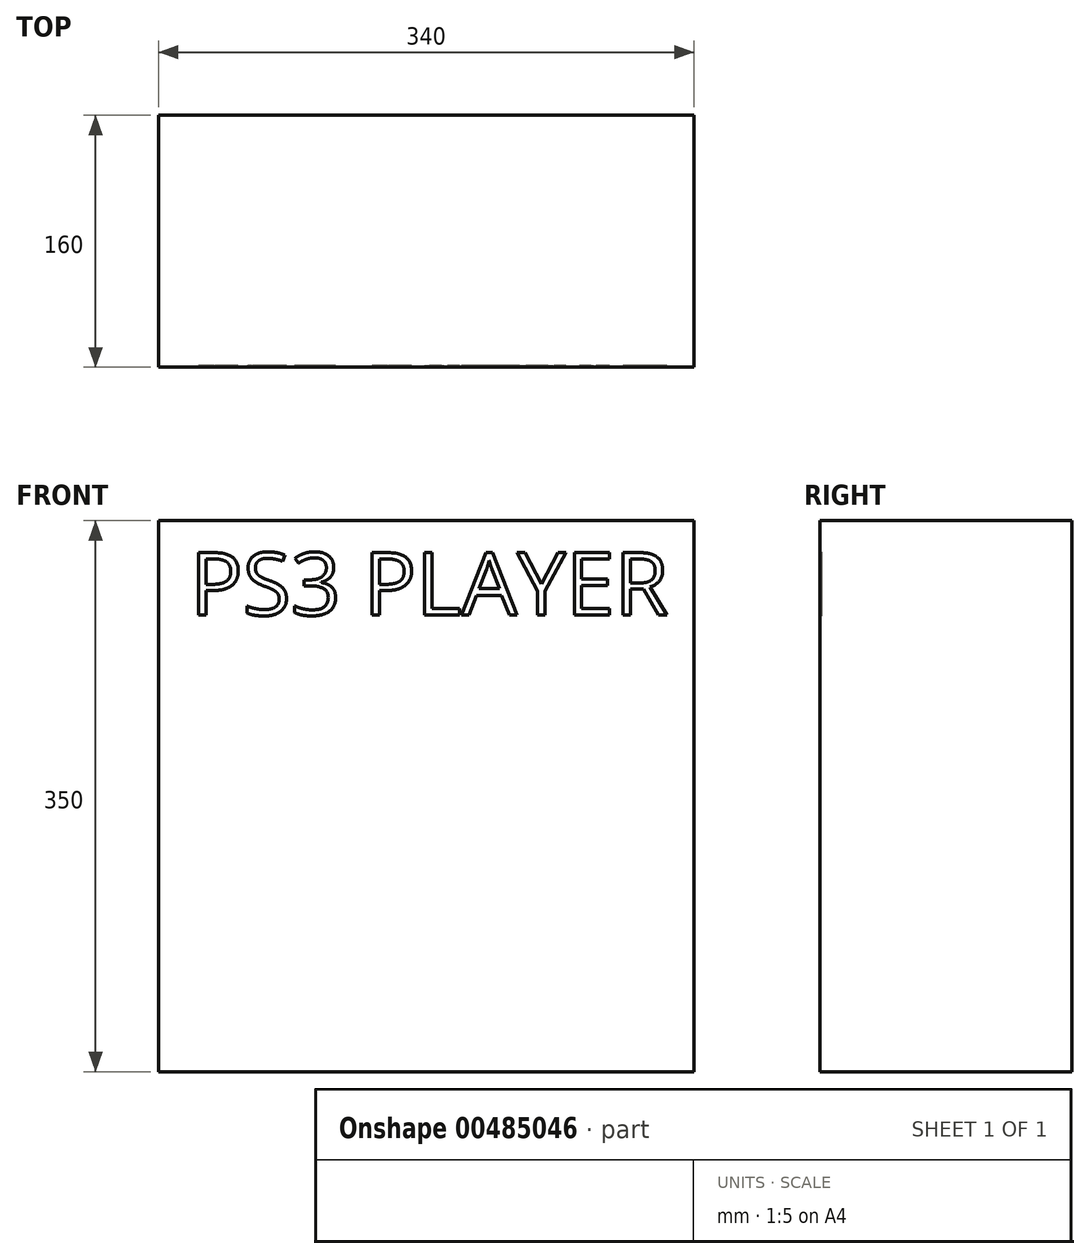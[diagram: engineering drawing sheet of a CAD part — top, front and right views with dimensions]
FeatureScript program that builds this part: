
annotation { "Feature Type Name" : "Feature", "Feature Type Description" : "" }
export const myFeature = defineFeature(function(context is Context, id is Id, definition is map)
    precondition{}
    {
        {
            var Q0;
            Q0=qCreatedBy(makeId("Top.planeOp"),FACE);
            var sketch = newSketch(context, id + "F0", { "sketchPlane" : qUnion([Q0])});
            skLineSegment(sketch, "E0.bottom", {"start": v(-170, -80) * mm, "end": v(170, -80) * mm});
            skLineSegment(sketch, "E0.top", {"start": v(-170, 80) * mm, "end": v(170, 80) * mm});
            skLineSegment(sketch, "E0.left", {"start": v(-170, -80) * mm, "end": v(-170, 80) * mm});
            skLineSegment(sketch, "E0.right", {"start": v(170, -80) * mm, "end": v(170, 80) * mm});
            skPoint(sketch, "E0.middle", {"position": v(0, 0) * mm});
            skSolve(sketch);
        }
        {
            var Q0;
            Q0=makeQuery(id+"F0.imprint","IMPRINT",FACE,{"disambiguationData":[TD([[makeQuery(id+"F0.imprint","IMPRINT",EDGE,{"derivedFrom":sQuery(id+"F0.wireOp",EDGE,"E0.bottom")}),1.0]])]});
            extrude(context, id + "F1", {"entities" : qUnion([Q0]), "depth" : 350 * mm});
        }
        {
            var Q0;
            Q0=makeQuery(id+"F1.opExtrude","SWEPT_FACE",FACE,{"disambiguationData":[OSD([sQuery(id+"F0.wireOp",EDGE,"E0.bottom")])]});
            var sketch = newSketch(context, id + "F2", { "sketchPlane" : qUnion([Q0])});
            skText(sketch, "E1", { "text": "PS3 PLAYER", "fontName": "OpenSans-Regular.ttf"});
            const initialGuessF2  = {"E1": [-0.15, 0.29, 1, 0, 0.04]};
            skSetInitialGuess(sketch, initialGuessF2);
            skSolve(sketch);
        }
        {
            var Q0;
            Q0 = qSketchRegion(id + "F2", true);
            extrude(context, id + "F3", {"entities" : qUnion([Q0]), "operationType" : NewBodyOperationType.REMOVE, "oppositeDirection" : true, "depth" : 1 * mm});
        }
    });
